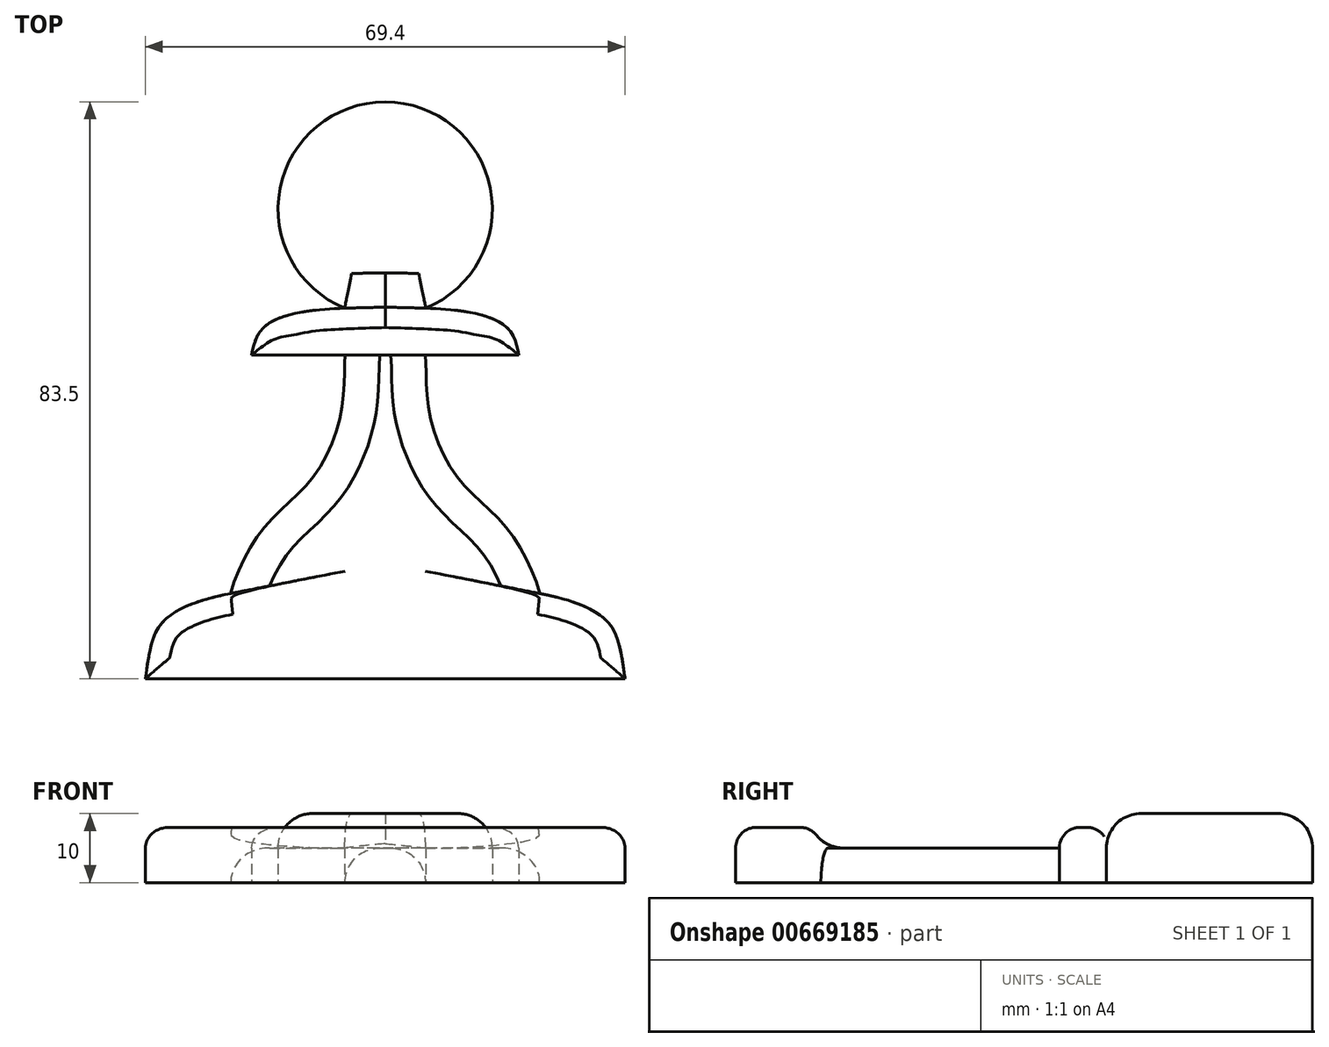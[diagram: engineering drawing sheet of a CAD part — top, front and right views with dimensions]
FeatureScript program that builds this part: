
annotation { "Feature Type Name" : "Feature", "Feature Type Description" : "" }
export const myFeature = defineFeature(function(context is Context, id is Id, definition is map)
    precondition{}
    {
        {
            var Q0;
            Q0=qCreatedBy(makeId("Top.planeOp"),FACE);
            var sketch = newSketch(context, id + "F0", { "sketchPlane" : qUnion([Q0])});
            skLineSegment(sketch, "E0", {"start": v(0, -73.68) * mm, "end": v(-34.7, -73.68) * mm});
            skFitSpline(sketch, "E1", {"points": [v(-34.7, -73.68) * mm, v(-31.85, -65.1) * mm, v(-22.36, -61.33) * mm], "startDerivative": vector(4.14, 32.34) * mm, "endDerivative": vector(28.48, 5.57) * mm});
            skFitSpline(sketch, "E2", {"points": [v(-22.36, -61.33) * mm, v(-17.41, -51.66) * mm, v(-10.57, -44.66) * mm, v(-6.27, -34.47) * mm, v(-5.82, -26.83) * mm], "startDerivative": vector(10.2, 37.72) * mm, "endDerivative": vector(2.16, 24.04) * mm});
            skLineSegment(sketch, "E3", {"start": v(0, -26.83) * mm, "end": v(-19.32, -26.83) * mm});
            skFitSpline(sketch, "E4", {"points": [v(-19.32, -26.83) * mm, v(-18.05, -23.33) * mm, v(-12.96, -20.79) * mm, v(0, -19.93) * mm], "startDerivative": vector(1.48, 9.94) * mm, "endDerivative": vector(42.06, 0.34) * mm});
            skCircle(sketch, "E5", {"center": v(0, -5.68) * mm, "radius": 15.5 * mm});
            skLineSegment(sketch, "E6.MirrorCS", {"start": v(0, -26.83) * mm, "end": v(19.32, -26.83) * mm});
            skFitSpline(sketch, "E7.MirrorCS", {"points": [v(19.32, -26.83) * mm, v(18.05, -23.33) * mm, v(12.96, -20.79) * mm, v(0, -19.93) * mm], "startDerivative": vector(-1.48, 9.94) * mm, "endDerivative": vector(-42.06, 0.34) * mm});
            skFitSpline(sketch, "E8.MirrorCS", {"points": [v(22.36, -61.33) * mm, v(17.41, -51.66) * mm, v(10.57, -44.66) * mm, v(6.27, -34.47) * mm, v(5.82, -26.83) * mm], "startDerivative": vector(-10.2, 37.72) * mm, "endDerivative": vector(-2.16, 24.04) * mm});
            skFitSpline(sketch, "E9.MirrorCS", {"points": [v(34.7, -73.68) * mm, v(31.85, -65.1) * mm, v(22.36, -61.33) * mm], "startDerivative": vector(-4.14, 32.34) * mm, "endDerivative": vector(-28.48, 5.57) * mm});
            skLineSegment(sketch, "E10.MirrorCS", {"start": v(0, -73.68) * mm, "end": v(34.7, -73.68) * mm});
            skLineSegment(sketch, "E11", {"start": v(-22.36, -61.33) * mm, "end": v(22.36, -61.33) * mm});
            skSolve(sketch);
        }
        {
            var Q0;
            {var subQ4=sQuery(id+"F0.wireOp",EDGE,"E2");Q0=makeQuery(id+"F0.imprint","IMPRINT",FACE,{"disambiguationData":[TD([[makeQuery(id+"F0.imprint","IMPRINT",EDGE,{"derivedFrom":subQ4}),-1.0]])]});}
            extrude(context, id + "F1", {"entities" : qUnion([Q0]), "depth" : 5 * mm, "offsetDistance" : 25 * mm});
        }
        {
            var Q0;
            {var subQ5=sQuery(id+"F0.wireOp",EDGE,"E3");var subQ7=makeQuery(id+"F0.imprint","INTERSECT",VERTEX,{"derivedFrom":[sQuery(id+"F0.wireOp",EDGE,"E2"),subQ5]});Q0=makeQuery(id+"F0.imprint","IMPRINT",FACE,{"disambiguationData":[TD([[makeQuery(id+"F0.imprint","IMPRINT",EDGE,{"disambiguationData":[TD([[subQ7,1.0]])],"derivedFrom":subQ5}),-1.0]])]});}
            var Q1;
            Q1=makeQuery(id+"F0.imprint","IMPRINT",FACE,{"disambiguationData":[TD([[makeQuery(id+"F0.imprint","IMPRINT",EDGE,{"derivedFrom":sQuery(id+"F0.wireOp",EDGE,"E0")}),-1.0]])]});
            var Q2;
            {var subQ0=sQuery(id+"F0.wireOp",EDGE,"E7.MirrorCS");var subQ1=sQuery(id+"F0.wireOp",EDGE,"E4");var subQ2=makeQuery(id+"F0.imprint","INTERSECT",VERTEX,{"derivedFrom":[subQ1,subQ0]});Q2=makeQuery(id+"F0.imprint","IMPRINT",FACE,{"disambiguationData":[TD([[makeQuery(id+"F0.imprint","IMPRINT",EDGE,{"disambiguationData":[TD([[subQ2,1.0]])],"derivedFrom":subQ1}),-1.0]])]});}
            extrude(context, id + "F2", {"entities" : qUnion([Q0, Q1, Q2]), "depth" : 8 * mm, "offsetDistance" : 25 * mm});
        }
        {
            var Q0;
            {var subQ0=sQuery(id+"F0.wireOp",EDGE,"E7.MirrorCS");var subQ1=sQuery(id+"F0.wireOp",EDGE,"E4");var subQ2=makeQuery(id+"F0.imprint","INTERSECT",VERTEX,{"derivedFrom":[subQ1,subQ0]});Q0=makeQuery(id+"F0.imprint","IMPRINT",FACE,{"disambiguationData":[TD([[makeQuery(id+"F0.imprint","IMPRINT",EDGE,{"disambiguationData":[TD([[subQ2,1.0]])],"derivedFrom":subQ1}),1.0]])]});}
            extrude(context, id + "F3", {"entities" : qUnion([Q0]), "depth" : 9 * mm, "offsetDistance" : 25 * mm});
        }
        {
            var Q0;
            Q0=makeQuery(id+"F3.opExtrude","SWEPT_BODY",BODY,{"disambiguationData":[OSD([sQuery(id+"F0.wireOp",EDGE,"E4"),sQuery(id+"F0.wireOp",EDGE,"E5"),sQuery(id+"F0.wireOp",EDGE,"E7.MirrorCS")])]});
            var Q1;
            Q1=makeQuery(id+"F2.opExtrude","SWEPT_BODY",BODY,{"disambiguationData":[OSD([sQuery(id+"F0.wireOp",EDGE,"E3"),sQuery(id+"F0.wireOp",EDGE,"E4"),sQuery(id+"F0.wireOp",EDGE,"E6.MirrorCS"),sQuery(id+"F0.wireOp",EDGE,"E7.MirrorCS")])]});
            var Q2;
            Q2=makeQuery(id+"F1.opExtrude","SWEPT_BODY",BODY,{"disambiguationData":[OSD([sQuery(id+"F0.wireOp",EDGE,"E2"),sQuery(id+"F0.wireOp",EDGE,"E3"),sQuery(id+"F0.wireOp",EDGE,"E6.MirrorCS"),sQuery(id+"F0.wireOp",EDGE,"E8.MirrorCS"),sQuery(id+"F0.wireOp",EDGE,"E11")])]});
            var Q3;
            Q3=makeQuery(id+"F2.opExtrude","SWEPT_BODY",BODY,{"disambiguationData":[OSD([sQuery(id+"F0.wireOp",EDGE,"E0"),sQuery(id+"F0.wireOp",EDGE,"E1"),sQuery(id+"F0.wireOp",EDGE,"E9.MirrorCS"),sQuery(id+"F0.wireOp",EDGE,"E10.MirrorCS"),sQuery(id+"F0.wireOp",EDGE,"E11")])]});
            booleanBodies(context, id + "F4", {"operationType" : BooleanOperationType.UNION, "tools" : qUnion([Q0, Q1, Q2, Q3])});
        }
        {
            var Q0;
            {var subQ0=sQuery(id+"F0.wireOp",EDGE,"E4");Q0=makeQuery(id+"F4.opBoolean","SPLIT",EDGE,{"disambiguationData":[topologyDisambiguationEdgeConnected([makeQuery(id+"F2.opExtrude","SWEPT_FACE",FACE,{"disambiguationData":[OSD([subQ0])]})])],"derivedFrom":makeQuery(id+"F2.opExtrude","CAP_EDGE",EDGE,{"disambiguationData":[OSD([subQ0])],"isStart":false})});}
            var Q1;
            {var subQ0=sQuery(id+"F0.wireOp",EDGE,"E7.MirrorCS");Q1=makeQuery(id+"F4.opBoolean","SPLIT",EDGE,{"disambiguationData":[topologyDisambiguationEdgeConnected([makeQuery(id+"F2.opExtrude","SWEPT_FACE",FACE,{"disambiguationData":[OSD([subQ0])]})])],"derivedFrom":makeQuery(id+"F2.opExtrude","CAP_EDGE",EDGE,{"disambiguationData":[OSD([subQ0])],"isStart":false})});}
            var Q2;
            Q2=makeQuery(id+"F2.opExtrude","CAP_EDGE",EDGE,{"disambiguationData":[OSD([sQuery(id+"F0.wireOp",EDGE,"E3"),sQuery(id+"F0.wireOp",EDGE,"E6.MirrorCS")])],"isStart":false});
            var Q3;
            Q3=makeQuery(id+"F2.opExtrude","CAP_EDGE",EDGE,{"disambiguationData":[OSD([sQuery(id+"F0.wireOp",EDGE,"E11")])],"isStart":false});
            var Q4;
            Q4=makeQuery(id+"F2.opExtrude","CAP_EDGE",EDGE,{"disambiguationData":[OSD([sQuery(id+"F0.wireOp",EDGE,"E1")])],"isStart":false});
            var Q5;
            Q5=makeQuery(id+"F2.opExtrude","CAP_EDGE",EDGE,{"disambiguationData":[OSD([sQuery(id+"F0.wireOp",EDGE,"E9.MirrorCS")])],"isStart":false});
            var Q6;
            Q6=makeQuery(id+"F2.opExtrude","CAP_EDGE",EDGE,{"disambiguationData":[OSD([sQuery(id+"F0.wireOp",EDGE,"E0"),sQuery(id+"F0.wireOp",EDGE,"E10.MirrorCS")])],"isStart":false});
            fillet(context, id + "F5", {"entities" : qUnion([Q0, Q1, Q2, Q3, Q4, Q5, Q6]), "radius" : 3 * mm, "tangentPropagation" : true, "allowEdgeOverflow" : false});
        }
        {
            var Q0;
            {var subQ0=sQuery(id+"F0.wireOp",EDGE,"E7.MirrorCS");var subQ1=sQuery(id+"F0.wireOp",EDGE,"E4");var subQ2=makeQuery(id+"F0.imprint","INTERSECT",VERTEX,{"derivedFrom":[subQ1,subQ0]});Q0=makeQuery(id+"F0.imprint","IMPRINT",FACE,{"disambiguationData":[TD([[makeQuery(id+"F0.imprint","IMPRINT",EDGE,{"disambiguationData":[TD([[subQ2,1.0]])],"derivedFrom":subQ1}),1.0]])]});}
            extrude(context, id + "F6", {"entities" : qUnion([Q0]), "operationType" : NewBodyOperationType.ADD, "depth" : 10 * mm, "offsetDistance" : 25 * mm});
        }
        {
            var Q0;
            Q0=makeQuery(id+"F6.opExtrude","CAP_EDGE",EDGE,{"disambiguationData":[OSD([sQuery(id+"F0.wireOp",EDGE,"E5")])],"isStart":false});
            var Q1;
            Q1=makeQuery(id+"F6.opExtrude","CAP_EDGE",EDGE,{"disambiguationData":[OSD([sQuery(id+"F0.wireOp",EDGE,"E4")])],"isStart":false});
            var Q2;
            Q2=makeQuery(id+"F6.opExtrude","CAP_EDGE",EDGE,{"disambiguationData":[OSD([sQuery(id+"F0.wireOp",EDGE,"E7.MirrorCS")])],"isStart":false});
            fillet(context, id + "F7", {"entities" : qUnion([Q0, Q1, Q2]), "radius" : 5 * mm, "tangentPropagation" : true, "allowEdgeOverflow" : false});
        }
        {
            var Q0;
            Q0=makeQuery(id+"F1.opExtrude","CAP_EDGE",EDGE,{"disambiguationData":[OSD([sQuery(id+"F0.wireOp",EDGE,"E2")])],"isStart":false});
            var Q1;
            Q1=makeQuery(id+"F1.opExtrude","CAP_EDGE",EDGE,{"disambiguationData":[OSD([sQuery(id+"F0.wireOp",EDGE,"E8.MirrorCS")])],"isStart":false});
            fillet(context, id + "F8", {"entities" : qUnion([Q0, Q1]), "radius" : 5 * mm, "tangentPropagation" : true, "allowEdgeOverflow" : false});
        }
        {
            var Q0;
            {var subQ0=sQuery(id+"F0.wireOp",EDGE,"E11");Q0=makeQuery(id+"F5.opFillet","BLEND_EDGE",EDGE,{"blendedFrom":[makeQuery(id+"F2.opExtrude","CAP_EDGE",EDGE,{"disambiguationData":[OSD([subQ0])],"isStart":false}),makeQuery(id+"F1.opExtrude","CAP_FACE",FACE,{"disambiguationData":[OSD([sQuery(id+"F0.wireOp",EDGE,"E2"),sQuery(id+"F0.wireOp",EDGE,"E3"),sQuery(id+"F0.wireOp",EDGE,"E6.MirrorCS"),sQuery(id+"F0.wireOp",EDGE,"E8.MirrorCS"),subQ0])],"isStart":false})],"blendedInto":[makeQuery(id+"F1.opExtrude","CAP_FACE",FACE,{"disambiguationData":[OSD([sQuery(id+"F0.wireOp",EDGE,"E2"),sQuery(id+"F0.wireOp",EDGE,"E3"),sQuery(id+"F0.wireOp",EDGE,"E6.MirrorCS"),sQuery(id+"F0.wireOp",EDGE,"E8.MirrorCS"),subQ0])],"isStart":false})]});}
            fillet(context, id + "F9", {"entities" : qUnion([Q0]), "radius" : 5 * mm, "tangentPropagation" : true, "allowEdgeOverflow" : false});
        }
    });
